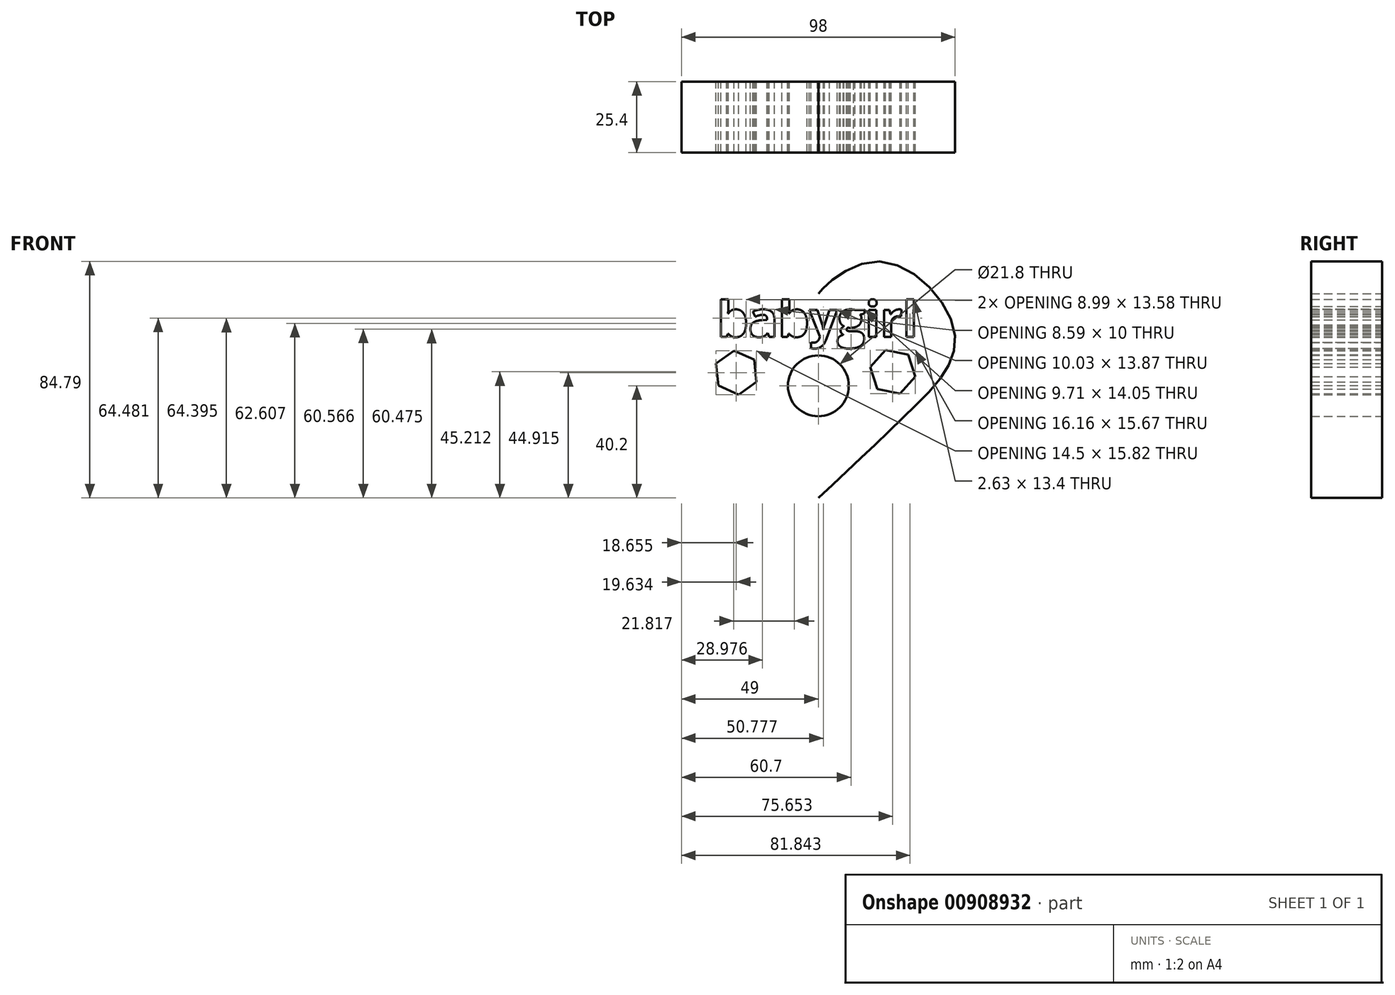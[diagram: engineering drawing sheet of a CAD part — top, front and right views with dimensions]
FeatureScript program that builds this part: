
annotation { "Feature Type Name" : "Feature", "Feature Type Description" : "" }
export const myFeature = defineFeature(function(context is Context, id is Id, definition is map)
    precondition{}
    {
        {
            var Q0;
            Q0=qCreatedBy(makeId("Front.planeOp"),FACE);
            var sketch = newSketch(context, id + "F0", { "sketchPlane" : qUnion([Q0])});
            skCircle(sketch, "E0", {"center": v(0, 0) * mm, "radius": 10.9 * mm});
            skFitSpline(sketch, "E1", {"points": [v(0, -40.2) * mm, v(-33.4, -8.49) * mm, v(-48.78, 19.14) * mm, v(-20.21, 44.57) * mm, v(0, 32.95) * mm, v(0, 32.64) * mm], "startDerivative": vector(-120.78, 113.06) * mm, "endDerivative": vector(-5.07, -8.78) * mm});
            skFitSpline(sketch, "E2.MirrorCS", {"points": [v(0, -40.2) * mm, v(33.4, -8.49) * mm, v(48.78, 19.14) * mm, v(20.21, 44.57) * mm, v(0, 32.95) * mm, v(0, 32.64) * mm], "startDerivative": vector(120.78, 113.06) * mm, "endDerivative": vector(5.07, -8.78) * mm});
            skText(sketch, "E3", { "text": "babygirl\n", "fontName": "OpenSans-Bold.ttf"});
            skCircle(sketch, "E4.cCircle", {"center": v(-29.37, 4.71) * mm, "radius": 6.89 * mm, "construction": true});
            skLineSegment(sketch, "E4.0", {"start": v(-30.17, 12.62) * mm, "end": v(-22.92, 9.36) * mm});
            skLineSegment(sketch, "E4.1", {"start": v(-22.92, 9.36) * mm, "end": v(-22.12, 1.45) * mm});
            skLineSegment(sketch, "E4.2", {"start": v(-22.12, 1.45) * mm, "end": v(-28.57, -3.2) * mm});
            skLineSegment(sketch, "E4.3", {"start": v(-28.57, -3.2) * mm, "end": v(-35.82, 0.07) * mm});
            skLineSegment(sketch, "E4.4", {"start": v(-35.82, 0.07) * mm, "end": v(-36.62, 7.98) * mm});
            skLineSegment(sketch, "E4.5", {"start": v(-36.62, 7.98) * mm, "end": v(-30.17, 12.62) * mm});
            skPoint(sketch, "E4.0.midPoint", {"position": v(-26.54, 11) * mm});
            skPoint(sketch, "E5.0.midPoint", {"position": v(9.58, 4.4) * mm});
            skPoint(sketch, "E6.0.midPoint", {"position": v(57.6, -12.47) * mm});
            skCircle(sketch, "E7.cCircle", {"center": v(26.65, 5.01) * mm, "radius": 7.15 * mm, "construction": true});
            skLineSegment(sketch, "E7.0", {"start": v(29.24, -2.82) * mm, "end": v(21.16, -1.15) * mm});
            skLineSegment(sketch, "E7.1", {"start": v(21.16, -1.15) * mm, "end": v(18.57, 6.69) * mm});
            skLineSegment(sketch, "E7.2", {"start": v(18.57, 6.69) * mm, "end": v(24.07, 12.85) * mm});
            skLineSegment(sketch, "E7.3", {"start": v(24.07, 12.85) * mm, "end": v(32.14, 11.17) * mm});
            skLineSegment(sketch, "E7.4", {"start": v(32.14, 11.17) * mm, "end": v(34.73, 3.34) * mm});
            skLineSegment(sketch, "E7.5", {"start": v(34.73, 3.34) * mm, "end": v(29.24, -2.82) * mm});
            skPoint(sketch, "E7.0.midPoint", {"position": v(25.2, -1.98) * mm});
            const initialGuessF0  = {"E3": [-0.03622, 0.01758, 1, 0, 0.0127]};
            skSetInitialGuess(sketch, initialGuessF0);
            skSolve(sketch);
        }
        {
            var Q0;
            Q0 = qSketchRegion(id + "F0", true);
            extrude(context, id + "F1", {"entities" : qUnion([Q0]), "depth" : 25.4 * mm, "offsetDistance" : 25.4 * mm});
        }
    });
